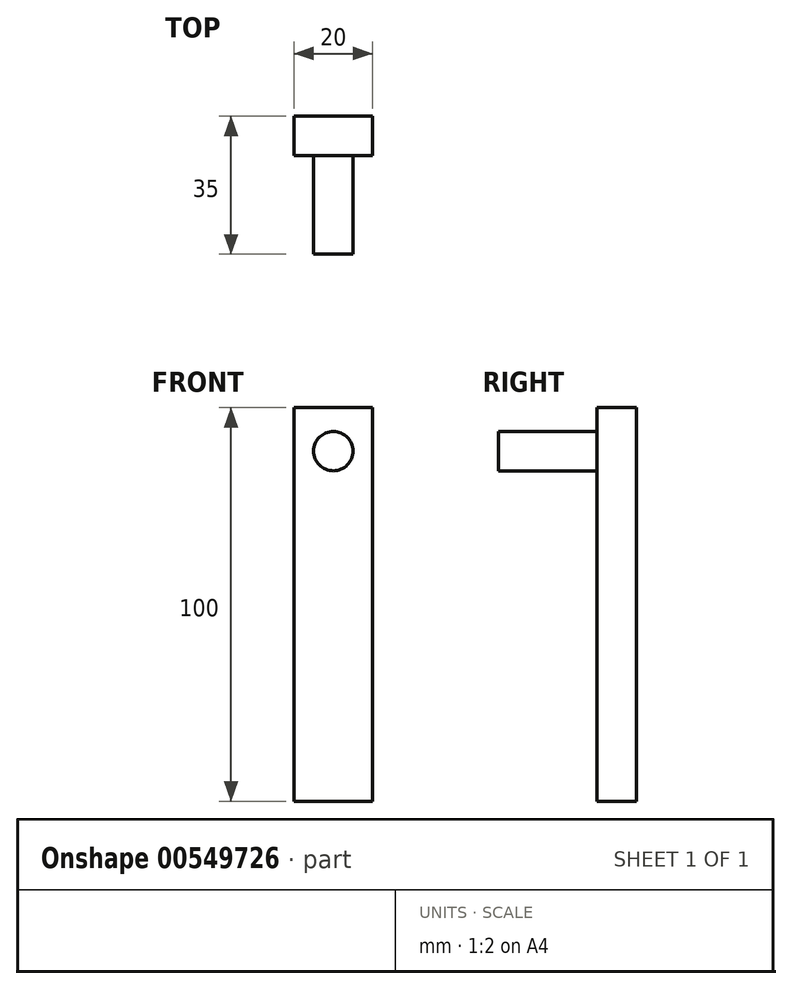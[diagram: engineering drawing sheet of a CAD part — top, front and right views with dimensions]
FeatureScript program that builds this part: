
annotation { "Feature Type Name" : "Feature", "Feature Type Description" : "" }
export const myFeature = defineFeature(function(context is Context, id is Id, definition is map)
    precondition{}
    {
        {
            var Q0;
            Q0=qCreatedBy(makeId("Front.planeOp"),FACE);
            var sketch = newSketch(context, id + "F0", { "sketchPlane" : qUnion([Q0])});
            skLineSegment(sketch, "E0.bottom", {"start": v(0, 0) * mm, "end": v(20, 0) * mm});
            skLineSegment(sketch, "E0.top", {"start": v(0, 100) * mm, "end": v(20, 100) * mm});
            skLineSegment(sketch, "E0.left", {"start": v(0, 0) * mm, "end": v(0, 100) * mm});
            skLineSegment(sketch, "E0.right", {"start": v(20, 0) * mm, "end": v(20, 100) * mm});
            skSolve(sketch);
        }
        {
            var Q0;
            Q0 = qSketchRegion(id + "F0", true);
            extrude(context, id + "F1", {"entities" : qUnion([Q0]), "depth" : 10 * mm, "offsetDistance" : 25 * mm});
        }
        {
            var Q0;
            Q0=makeQuery(id+"F1.opExtrude","CAP_FACE",FACE,{"disambiguationData":[OSD([sQuery(id+"F0.wireOp",EDGE,"E0.bottom"),sQuery(id+"F0.wireOp",EDGE,"E0.top"),sQuery(id+"F0.wireOp",EDGE,"E0.left"),sQuery(id+"F0.wireOp",EDGE,"E0.right")])],"isStart":false});
            var sketch = newSketch(context, id + "F2", { "sketchPlane" : qUnion([Q0])});
            skLineSegment(sketch, "E1", {"start": v(10, 100) * mm, "end": v(10, 88.95) * mm, "construction": true});
            skCircle(sketch, "E2", {"center": v(10, 88.95) * mm, "radius": 5 * mm});
            skSolve(sketch);
        }
        {
            var Q0;
            Q0=makeQuery(id+"F2.imprint","IMPRINT",FACE,{"disambiguationData":[TD([[makeQuery(id+"F2.imprint","IMPRINT",EDGE,{"derivedFrom":sQuery(id+"F2.wireOp",EDGE,"E2")}),1.0]])]});
            extrude(context, id + "F3", {"entities" : qUnion([Q0]), "operationType" : NewBodyOperationType.ADD, "depth" : 25 * mm, "offsetDistance" : 25 * mm});
        }
    });
